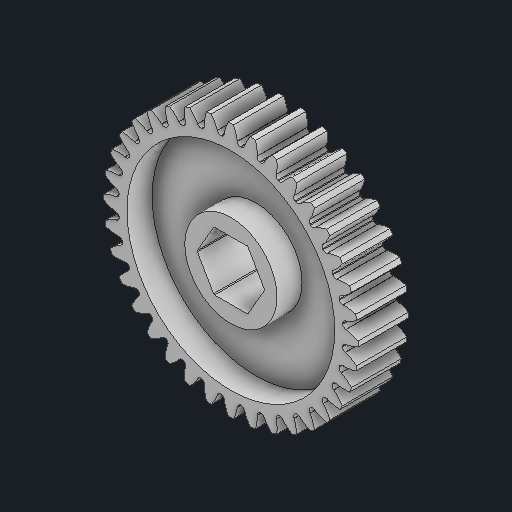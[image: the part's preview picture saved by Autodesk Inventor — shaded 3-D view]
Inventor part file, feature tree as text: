
AUTODESK INVENTOR PART (.ipt)
format: ipt  version: 2024.2 (Build 282272000, 272)  size: 1,416,192 bytes
history: native  units: in
note: dims shown in document units (in); Inventor stores cm internally (conversion verified against a paired STEP export)
features: extrude x3, sketch x3, other x3
ambient origin geometry x8: Origin, YZ Plane, XZ Plane, XY Plane, X Axis, Y Axis, Z Axis, Center Point
bodies: Solid1 (feature_tree), Solid2 (feature_tree), Solid3 (feature_tree)
feature tree (9):
  extrude  "Extrusion1"  Depth=1.0in TaperAngle=0.0deg
  extrude  "Extrusion2"  Depth=1.0in TaperAngle=0.0deg
  extrude  "Extrusion3"  Depth=1.0in TaperAngle=0.0deg
  sketch  "Sketch1"  dims[d0=1.0in d1=1.0in d2=0.0in]
  sketch  "Sketch2"  dims[d3=0.25in d4=1.0in d5=0.0in]
  sketch  "Sketch3"  dims[d6=0.25in d7=1.0in d8=0.0in]
  other  "2303-4008-0036_Gear Blank_1:1"
  other  "2806-0005-0004_91390A117_2:1"
  other  "2806-0005-0004_91390A117_3:1"
